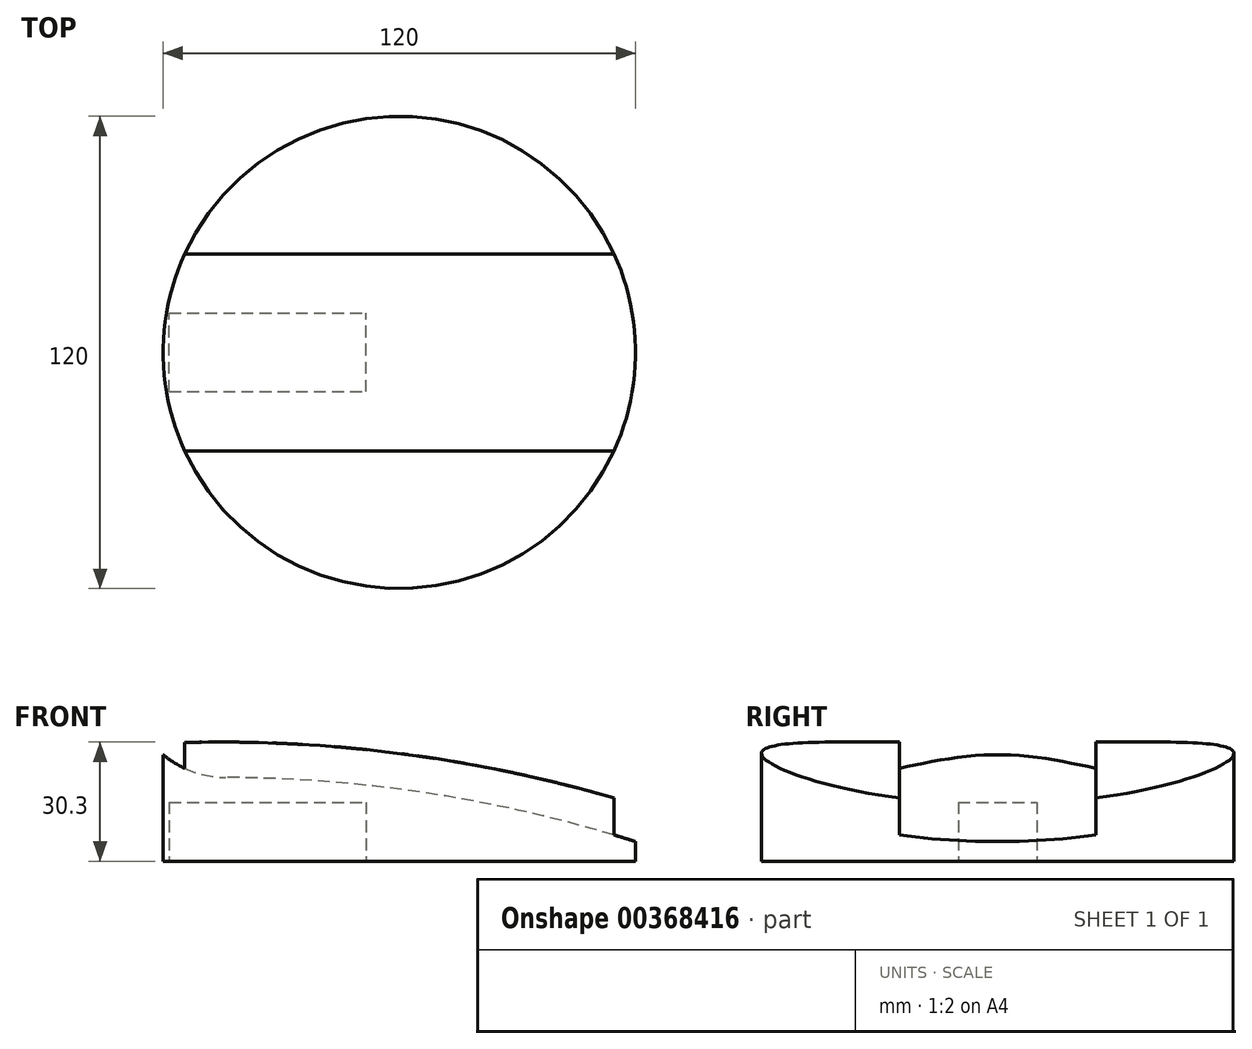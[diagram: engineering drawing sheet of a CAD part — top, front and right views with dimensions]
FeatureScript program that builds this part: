
annotation { "Feature Type Name" : "Feature", "Feature Type Description" : "" }
export const myFeature = defineFeature(function(context is Context, id is Id, definition is map)
    precondition{}
    {
        {
            var Q0;
            Q0=qCreatedBy(makeId("Top.planeOp"),FACE);
            var sketch = newSketch(context, id + "F0", { "sketchPlane" : qUnion([Q0])});
            skCircle(sketch, "E0", {"center": v(0, 0) * mm, "radius": 60 * mm});
            skSolve(sketch);
        }
        {
            var Q0;
            Q0=makeQuery(id+"F0.imprint","IMPRINT",FACE,{"disambiguationData":[TD([[makeQuery(id+"F0.imprint","IMPRINT",EDGE,{"derivedFrom":sQuery(id+"F0.wireOp",EDGE,"E0")}),1.0]])]});
            extrude(context, id + "F1", {"entities" : qUnion([Q0]), "depth" : 40 * mm});
        }
        {
            var Q0;
            Q0=qCreatedBy(makeId("Front.planeOp"),FACE);
            var sketch = newSketch(context, id + "F2", { "sketchPlane" : qUnion([Q0])});
            skArc(sketch, "E1", {"start": v(60, 5) * mm, "mid": v(0.7, 18.23) * mm, "end": v(-60, 21) * mm});
            skArc(sketch, "E2.0", {"start": v(60, 14.43) * mm, "mid": v(0.66, 27.31) * mm, "end": v(-60, 30) * mm});
            skLineSegment(sketch, "E3", {"start": v(-60, 21) * mm, "end": v(-60, 41.47) * mm});
            skLineSegment(sketch, "E4", {"start": v(-60, 41.47) * mm, "end": v(60, 41.47) * mm});
            skLineSegment(sketch, "E5", {"start": v(60, 41.47) * mm, "end": v(60, 5) * mm});
            skArc(sketch, "E6", {"start": v(-60, 21) * mm, "mid": v(-80.77, 141.4) * mm, "end": v(-31, 253) * mm});
            skArc(sketch, "E7", {"start": v(-67.21, 36.96) * mm, "mid": v(-56.93, 24.88) * mm, "end": v(-41.44, 21.43) * mm});
            skSolve(sketch);
        }
        {
            var Q0;
            {var subQ0=sQuery(id+"F2.wireOp",EDGE,"E2.0");Q0=makeQuery(id+"F2.imprint","IMPRINT",FACE,{"disambiguationData":[TD([[makeQuery(id+"F2.imprint","IMPRINT",EDGE,{"derivedFrom":subQ0}),-1.0]])]});}
            extrude(context, id + "F3", {"entities" : qUnion([Q0]), "operationType" : NewBodyOperationType.REMOVE, "endBound" : BoundingType.SYMMETRIC, "oppositeDirection" : true, "depth" : 200 * mm});
        }
        {
            var Q0;
            {var subQ3=sQuery(id+"F2.wireOp",EDGE,"E2.0");Q0=makeQuery(id+"F2.imprint","IMPRINT",FACE,{"disambiguationData":[TD([[makeQuery(id+"F2.imprint","IMPRINT",EDGE,{"derivedFrom":subQ3}),1.0]])]});}
            extrude(context, id + "F4", {"entities" : qUnion([Q0]), "operationType" : NewBodyOperationType.REMOVE, "endBound" : BoundingType.SYMMETRIC, "oppositeDirection" : true, "depth" : 50 * mm});
        }
        {
            var Q0;
            Q0=makeQuery(id+"F1.opExtrude","CAP_FACE",FACE,{"disambiguationData":[OSD([sQuery(id+"F0.wireOp",EDGE,"E0")])],"isStart":true});
            var sketch = newSketch(context, id + "F5", { "sketchPlane" : qUnion([Q0])});
            skLineSegment(sketch, "E8.bottom", {"start": v(-58.5, 10) * mm, "end": v(-8.5, 10) * mm});
            skLineSegment(sketch, "E8.top", {"start": v(-58.5, -10) * mm, "end": v(-8.5, -10) * mm});
            skLineSegment(sketch, "E8.left", {"start": v(-58.5, 10) * mm, "end": v(-58.5, -10) * mm});
            skLineSegment(sketch, "E8.right", {"start": v(-8.5, 10) * mm, "end": v(-8.5, -10) * mm});
            skLineSegment(sketch, "E9", {"start": v(-8.5, 0) * mm, "end": v(0, 0) * mm, "construction": true});
            skSolve(sketch);
        }
        {
            var Q0;
            Q0=makeQuery(id+"F5.imprint","IMPRINT",FACE,{"disambiguationData":[TD([[makeQuery(id+"F5.imprint","IMPRINT",EDGE,{"derivedFrom":sQuery(id+"F5.wireOp",EDGE,"E8.bottom")}),-1.0]])]});
            extrude(context, id + "F6", {"entities" : qUnion([Q0]), "operationType" : NewBodyOperationType.REMOVE, "oppositeDirection" : true, "depth" : 15 * mm});
        }
    });
